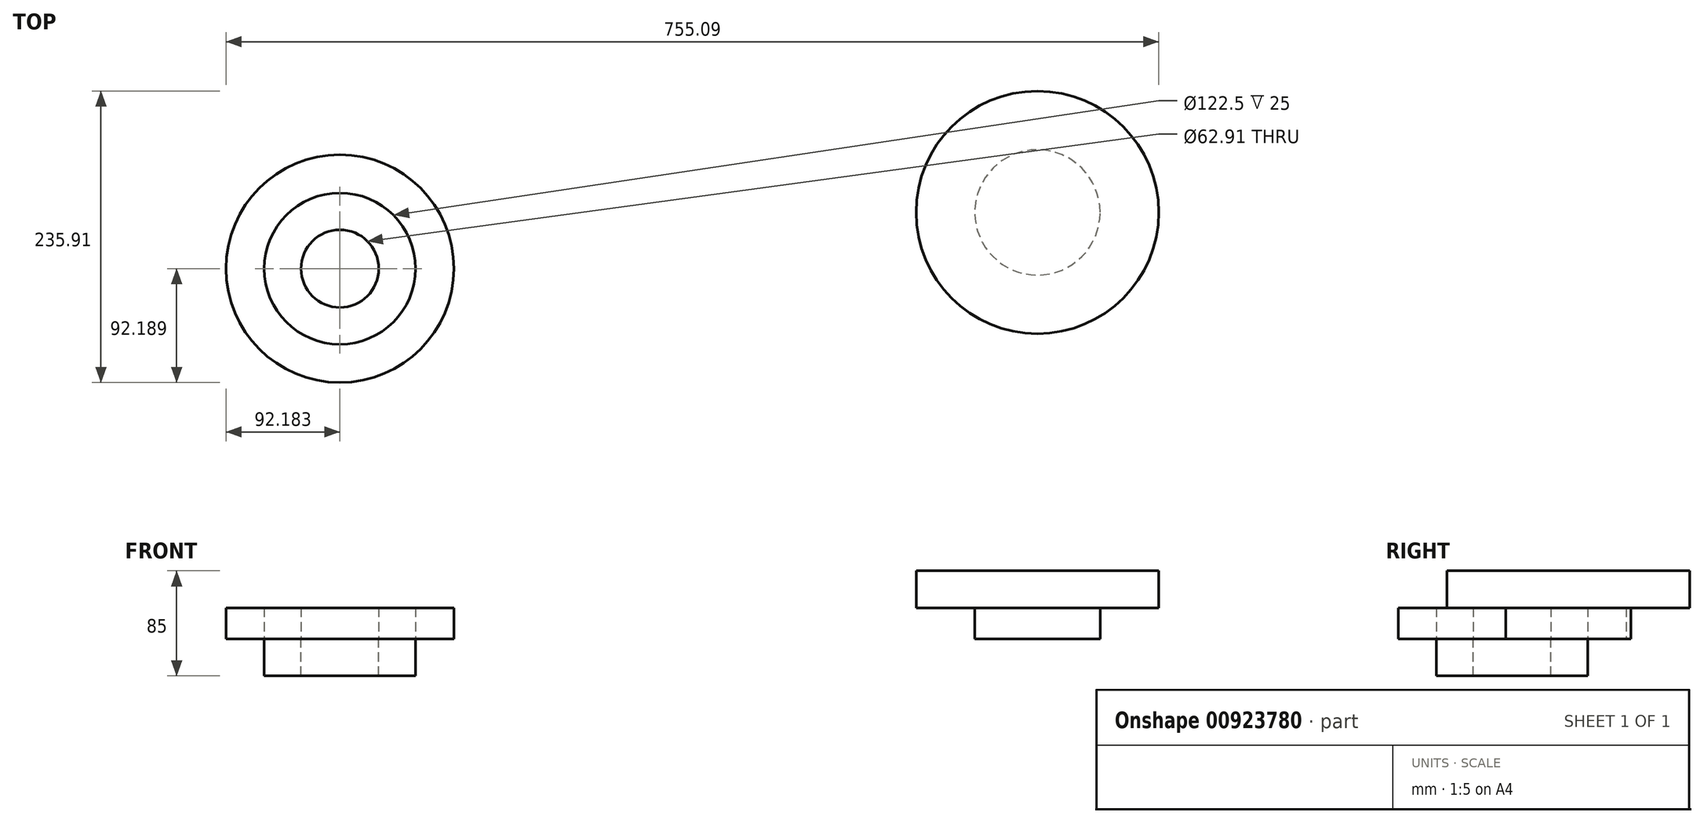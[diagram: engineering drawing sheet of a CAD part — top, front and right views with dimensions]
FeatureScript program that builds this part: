
annotation { "Feature Type Name" : "Feature", "Feature Type Description" : "" }
export const myFeature = defineFeature(function(context is Context, id is Id, definition is map)
    precondition{}
    {
        {
            var Q0;
            Q0=qCreatedBy(makeId("Top.planeOp"),FACE);
            var sketch = newSketch(context, id + "F0", { "sketchPlane" : qUnion([Q0])});
            skCircle(sketch, "E0", {"center": v(49.9, 57.32) * mm, "radius": 40.24 * mm});
            skCircle(sketch, "E1", {"center": v(64.75, 73.82) * mm, "radius": 98.2 * mm});
            skSolve(sketch);
        }
        {
            var Q0;
            Q0=makeQuery(id+"F0.imprint","IMPRINT",FACE,{"disambiguationData":[TD([[makeQuery(id+"F0.imprint","IMPRINT",EDGE,{"derivedFrom":sQuery(id+"F0.wireOp",EDGE,"E0")}),1.0]])]});
            var Q1;
            Q1=makeQuery(id+"F0.imprint","IMPRINT",FACE,{"disambiguationData":[TD([[makeQuery(id+"F0.imprint","IMPRINT",EDGE,{"derivedFrom":sQuery(id+"F0.wireOp",EDGE,"E0")}),-1.0]])]});
            extrude(context, id + "F1", {"entities" : qUnion([Q0, Q1]), "depth" : 30 * mm, "offsetDistance" : 25 * mm});
        }
        {
            var Q0;
            Q0=makeQuery(id+"F1.opExtrude","CAP_FACE",FACE,{"disambiguationData":[OSD([sQuery(id+"F0.wireOp",EDGE,"E1")])],"isStart":true});
            var sketch = newSketch(context, id + "F2", { "sketchPlane" : qUnion([Q0])});
            skCircle(sketch, "E2", {"center": v(64.75, -73.82) * mm, "radius": 50.75 * mm});
            skSolve(sketch);
        }
        {
            var Q0;
            Q0 = qSketchRegion(id + "F2", true);
            extrude(context, id + "F3", {"entities" : qUnion([Q0]), "operationType" : NewBodyOperationType.ADD, "depth" : 25 * mm, "offsetDistance" : 25 * mm});
        }
        {
            var Q0;
            Q0=makeQuery(id+"F3.opExtrude","CAP_FACE",FACE,{"disambiguationData":[OSD([sQuery(id+"F2.wireOp",EDGE,"E2")])],"isStart":false});
            var sketch = newSketch(context, id + "F4", { "sketchPlane" : qUnion([Q0])});
            skCircle(sketch, "E3", {"center": v(-499.97, -28.3) * mm, "radius": 31.46 * mm});
            skCircle(sketch, "E4", {"center": v(-499.97, -28.3) * mm, "radius": 61.25 * mm});
            skSolve(sketch);
        }
        {
            var Q0;
            Q0 = qSketchRegion(id + "F4", true);
            extrude(context, id + "F5", {"entities" : qUnion([Q0]), "depth" : 30 * mm, "offsetDistance" : 25 * mm});
        }
        {
            var Q0;
            Q0=makeQuery(id+"F5.opExtrude","CAP_FACE",FACE,{"disambiguationData":[OSD([sQuery(id+"F4.wireOp",EDGE,"E3"),sQuery(id+"F4.wireOp",EDGE,"E4")])],"isStart":true});
            var sketch = newSketch(context, id + "F6", { "sketchPlane" : qUnion([Q0])});
            skCircle(sketch, "E5", {"center": v(-499.97, 28.3) * mm, "radius": 92.19 * mm});
            skSolve(sketch);
        }
        {
            var Q0;
            Q0=makeQuery(id+"F6.imprint","IMPRINT",FACE,{"disambiguationData":[TD([[makeQuery(id+"F6.imprint","IMPRINT",EDGE,{"derivedFrom":sQuery(id+"F6.wireOp",EDGE,"E5")}),1.0]])]});
            var Q1;
            Q1=makeQuery(id+"F6.imprint","IMPRINT",FACE,{"disambiguationData":[TD([[makeQuery(id+"F6.imprint","IMPRINT",EDGE,{"derivedFrom":makeQuery(id+"F5.opExtrude","CAP_EDGE",EDGE,{"disambiguationData":[OSD([sQuery(id+"F4.wireOp",EDGE,"E3")])],"isStart":true})}),-1.0]])]});
            extrude(context, id + "F7", {"entities" : qUnion([Q0, Q1]), "depth" : 25 * mm, "offsetDistance" : 25 * mm});
        }
    });
